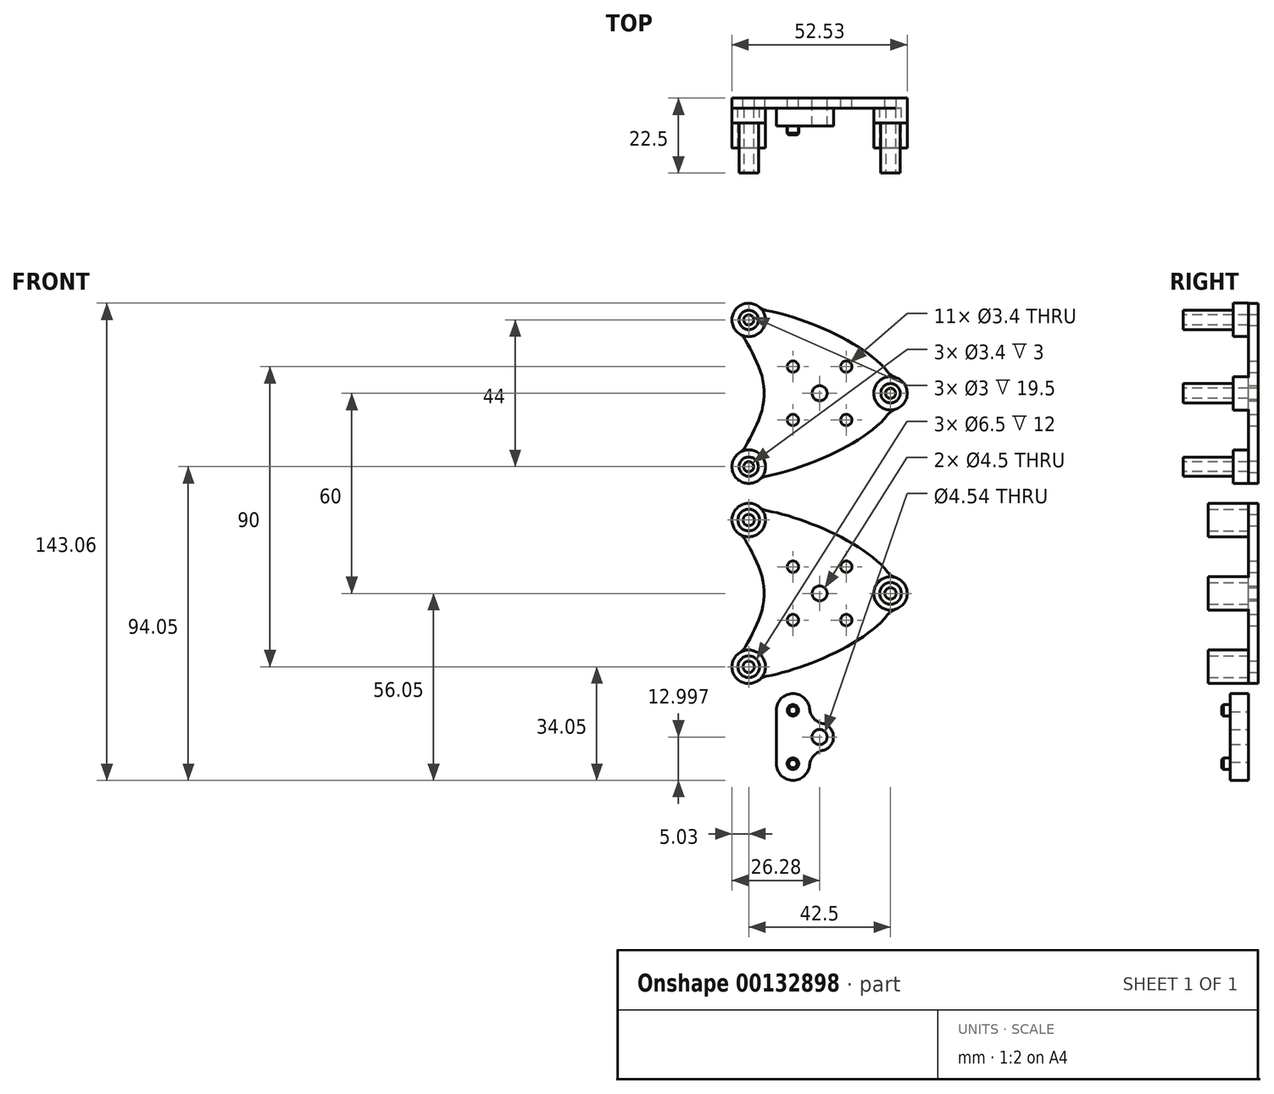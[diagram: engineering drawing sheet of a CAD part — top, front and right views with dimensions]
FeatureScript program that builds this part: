
annotation { "Feature Type Name" : "Feature", "Feature Type Description" : "" }
export const myFeature = defineFeature(function(context is Context, id is Id, definition is map)
    precondition{}
    {
        {
            var Q0;
            Q0=qCreatedBy(makeId("Front.planeOp"),FACE);
            var sketch = newSketch(context, id + "F0", { "sketchPlane" : qUnion([Q0])});
            skLineSegment(sketch, "E0", {"start": v(-21.25, 41.21) * mm, "end": v(-21.25, -41.21) * mm, "construction": true});
            skLineSegment(sketch, "E1", {"start": v(21.25, 41.21) * mm, "end": v(21.25, -41.21) * mm, "construction": true});
            skCircle(sketch, "E2", {"center": v(21.25, 0) * mm, "radius": 15.31 * mm, "construction": true});
            skPoint(sketch, "E2.centerSnap0", {"position": v(21.25, 0) * mm});
            skCircle(sketch, "E3", {"center": v(-21.25, 22) * mm, "radius": 15.31 * mm, "construction": true});
            skCircle(sketch, "E4", {"center": v(-21.25, -22) * mm, "radius": 15.31 * mm, "construction": true});
            skFitSpline(sketch, "E5", {"points": [v(-24.16, 24.83) * mm, v(22.95, 0) * mm, v(-24.16, -24.83) * mm, v(-16.56, 0) * mm, v(-24.16, 24.83) * mm]});
            skPoint(sketch, "E6", {"position": v(-54.58, 1.18) * mm});
            skPoint(sketch, "E7", {"position": v(-21.25, 0) * mm});
            skCircle(sketch, "E8", {"center": v(0, 0) * mm, "radius": 2.25 * mm});
            skCircle(sketch, "E9", {"center": v(-21.25, 22) * mm, "radius": 1.7 * mm});
            skCircle(sketch, "E10", {"center": v(-21.25, -22) * mm, "radius": 1.7 * mm});
            skCircle(sketch, "E11", {"center": v(21.25, 0) * mm, "radius": 1.7 * mm});
            skCircle(sketch, "E12", {"center": v(-21.25, -22) * mm, "radius": 3.5 * mm, "construction": true});
            skCircle(sketch, "E13", {"center": v(-8, 8) * mm, "radius": 1.7 * mm});
            skCircle(sketch, "E14.1.0.0", {"center": v(8, 8) * mm, "radius": 1.7 * mm});
            skLineSegment(sketch, "E14.direction1", {"start": v(-8, 8) * mm, "end": v(8, 8) * mm, "construction": true});
            skCircle(sketch, "E15.MirrorC", {"center": v(8, -8) * mm, "radius": 1.7 * mm});
            skCircle(sketch, "E16.MirrorC", {"center": v(-8, -8) * mm, "radius": 1.7 * mm});
            skCircle(sketch, "E17", {"center": v(-21.25, 22) * mm, "radius": 5 * mm});
            skCircle(sketch, "E18", {"center": v(-21.25, -22) * mm, "radius": 5 * mm});
            skCircle(sketch, "E19", {"center": v(21.25, 0) * mm, "radius": 5 * mm});
            skLineSegment(sketch, "E20.bottom", {"start": v(-10, 64.85) * mm, "end": v(10, 64.85) * mm, "construction": true});
            skLineSegment(sketch, "E20.top", {"start": v(-10, -64.85) * mm, "end": v(10, -64.85) * mm, "construction": true});
            skLineSegment(sketch, "E20.left", {"start": v(-10, 64.85) * mm, "end": v(-10, -64.85) * mm, "construction": true});
            skLineSegment(sketch, "E20.right", {"start": v(10, 64.85) * mm, "end": v(10, -64.85) * mm, "construction": true});
            skSolve(sketch);
        }
        {
            var Q0;
            Q0 = qSketchRegion(id + "F0", true);
            extrude(context, id + "F1", {"entities" : qUnion([Q0]), "depth" : 3 * mm});
        }
        {
            var Q0;
            {var subQ0=sQuery(id+"F0.wireOp",EDGE,"E19");var subQ1=sQuery(id+"F0.wireOp",EDGE,"E5");Q0=makeQuery(id+"F1.opExtrude","SWEPT_EDGE",EDGE,{"disambiguationData":[OSD([subQ1,subQ0]),TDD([makeQuery(id+"F0.imprint","INTERSECT",VERTEX,{"disambiguationData":[OD(1.0)],"derivedFrom":[subQ1,subQ0]})])]});}
            var Q1;
            {var subQ0=sQuery(id+"F0.wireOp",EDGE,"E19");var subQ1=sQuery(id+"F0.wireOp",EDGE,"E5");Q1=makeQuery(id+"F1.opExtrude","SWEPT_EDGE",EDGE,{"disambiguationData":[OSD([subQ1,subQ0]),TDD([makeQuery(id+"F0.imprint","INTERSECT",VERTEX,{"disambiguationData":[OD(0.0)],"derivedFrom":[subQ1,subQ0]})])]});}
            var Q2;
            {var subQ0=sQuery(id+"F0.wireOp",EDGE,"E17");var subQ1=sQuery(id+"F0.wireOp",EDGE,"E5");Q2=makeQuery(id+"F1.opExtrude","SWEPT_EDGE",EDGE,{"disambiguationData":[OSD([subQ1,subQ0]),TDD([makeQuery(id+"F0.imprint","INTERSECT",VERTEX,{"disambiguationData":[OD(1.0)],"derivedFrom":[subQ1,subQ0]})])]});}
            var Q3;
            {var subQ0=sQuery(id+"F0.wireOp",EDGE,"E18");var subQ1=sQuery(id+"F0.wireOp",EDGE,"E5");Q3=makeQuery(id+"F1.opExtrude","SWEPT_EDGE",EDGE,{"disambiguationData":[OSD([subQ1,subQ0]),TDD([makeQuery(id+"F0.imprint","INTERSECT",VERTEX,{"disambiguationData":[OD(1.0)],"derivedFrom":[subQ1,subQ0]})])]});}
            var Q4;
            {var subQ0=sQuery(id+"F0.wireOp",EDGE,"E18");var subQ1=sQuery(id+"F0.wireOp",EDGE,"E5");Q4=makeQuery(id+"F1.opExtrude","SWEPT_EDGE",EDGE,{"disambiguationData":[OSD([subQ1,subQ0]),TDD([makeQuery(id+"F0.imprint","INTERSECT",VERTEX,{"disambiguationData":[OD(0.0)],"derivedFrom":[subQ1,subQ0]})])]});}
            var Q5;
            {var subQ0=sQuery(id+"F0.wireOp",EDGE,"E17");var subQ1=sQuery(id+"F0.wireOp",EDGE,"E5");Q5=makeQuery(id+"F1.opExtrude","SWEPT_EDGE",EDGE,{"disambiguationData":[OSD([subQ1,subQ0]),TDD([makeQuery(id+"F0.imprint","INTERSECT",VERTEX,{"disambiguationData":[OD(0.0)],"derivedFrom":[subQ1,subQ0]})])]});}
            fillet(context, id + "F2", {"entities" : qUnion([Q0, Q1, Q2, Q3, Q4, Q5]), "radius" : 5 * mm, "tangentPropagation" : true, "allowEdgeOverflow" : false});
        }
        {
            var Q0;
            Q0=makeQuery(id+"F1.opExtrude","CAP_FACE",FACE,{"disambiguationData":[OSD([sQuery(id+"F0.wireOp",EDGE,"E5"),sQuery(id+"F0.wireOp",EDGE,"E8"),sQuery(id+"F0.wireOp",EDGE,"E9"),sQuery(id+"F0.wireOp",EDGE,"E10"),sQuery(id+"F0.wireOp",EDGE,"E11"),sQuery(id+"F0.wireOp",EDGE,"E13"),sQuery(id+"F0.wireOp",EDGE,"E14.1.0.0"),sQuery(id+"F0.wireOp",EDGE,"E15.MirrorC"),sQuery(id+"F0.wireOp",EDGE,"E16.MirrorC"),sQuery(id+"F0.wireOp",EDGE,"E17"),sQuery(id+"F0.wireOp",EDGE,"E18"),sQuery(id+"F0.wireOp",EDGE,"E19")])],"isStart":false});
            var sketch = newSketch(context, id + "F3", { "sketchPlane" : qUnion([Q0])});
            skCircle(sketch, "E21", {"center": v(-8, -35.05) * mm, "radius": 5 * mm});
            skCircle(sketch, "E22", {"center": v(-8, -51.05) * mm, "radius": 5 * mm});
            skLineSegment(sketch, "E23", {"start": v(-12.98, -35.46) * mm, "end": v(-12.98, -51.46) * mm});
            skLineSegment(sketch, "E24", {"start": v(-3, -34.97) * mm, "end": v(-3, -51.05) * mm});
            skCircle(sketch, "E25", {"center": v(-8, -35.05) * mm, "radius": 1.7 * mm});
            skCircle(sketch, "E26", {"center": v(-8, -51.05) * mm, "radius": 1.73 * mm});
            skCircle(sketch, "E27", {"center": v(0, -43.05) * mm, "radius": 4.14 * mm});
            skCircle(sketch, "E28", {"center": v(0, -43.05) * mm, "radius": 2.27 * mm});
            skSolve(sketch);
        }
        {
            var Q0;
            Q0 = qSketchRegion(id + "F3", true);
            extrude(context, id + "F4", {"entities" : qUnion([Q0]), "depth" : 5.4 * mm});
        }
        {
            var Q0;
            {var subQ0=sQuery(id+"F3.wireOp",EDGE,"E27");var subQ1=sQuery(id+"F3.wireOp",EDGE,"E24");Q0=makeQuery(id+"F4.opExtrude","SWEPT_EDGE",EDGE,{"disambiguationData":[OSD([subQ1,subQ0]),TDD([makeQuery(id+"F3.imprint","INTERSECT",VERTEX,{"disambiguationData":[OD(1.0)],"derivedFrom":[subQ1,subQ0]})])]});}
            var Q1;
            {var subQ0=sQuery(id+"F3.wireOp",EDGE,"E27");var subQ1=sQuery(id+"F3.wireOp",EDGE,"E24");Q1=makeQuery(id+"F4.opExtrude","SWEPT_EDGE",EDGE,{"disambiguationData":[OSD([subQ1,subQ0]),TDD([makeQuery(id+"F3.imprint","INTERSECT",VERTEX,{"disambiguationData":[OD(0.0)],"derivedFrom":[subQ1,subQ0]})])]});}
            fillet(context, id + "F5", {"entities" : qUnion([Q0, Q1]), "radius" : 5 * mm, "tangentPropagation" : true, "allowEdgeOverflow" : false});
        }
        {
            var Q0;
            Q0=makeQuery(id+"F1.opExtrude","SWEPT_BODY",BODY,{"disambiguationData":[OSD([sQuery(id+"F0.wireOp",EDGE,"E5"),sQuery(id+"F0.wireOp",EDGE,"E8"),sQuery(id+"F0.wireOp",EDGE,"E9"),sQuery(id+"F0.wireOp",EDGE,"E10"),sQuery(id+"F0.wireOp",EDGE,"E11"),sQuery(id+"F0.wireOp",EDGE,"E13"),sQuery(id+"F0.wireOp",EDGE,"E14.1.0.0"),sQuery(id+"F0.wireOp",EDGE,"E15.MirrorC"),sQuery(id+"F0.wireOp",EDGE,"E16.MirrorC"),sQuery(id+"F0.wireOp",EDGE,"E17"),sQuery(id+"F0.wireOp",EDGE,"E18"),sQuery(id+"F0.wireOp",EDGE,"E19")])]});
            transform(context, id + "F6", {"entities" : qUnion([Q0]), "transformType" : TransformType.TRANSLATION_3D, "dx" : 0 * mm, "dy" : 0 * mm, "dz" : 60 * mm, "makeCopy" : true});
        }
        {
            var Q0;
            Q0=makeQuery(id+"F1.opExtrude","CAP_FACE",FACE,{"disambiguationData":[OSD([sQuery(id+"F0.wireOp",EDGE,"E5"),sQuery(id+"F0.wireOp",EDGE,"E8"),sQuery(id+"F0.wireOp",EDGE,"E9"),sQuery(id+"F0.wireOp",EDGE,"E10"),sQuery(id+"F0.wireOp",EDGE,"E11"),sQuery(id+"F0.wireOp",EDGE,"E13"),sQuery(id+"F0.wireOp",EDGE,"E14.1.0.0"),sQuery(id+"F0.wireOp",EDGE,"E15.MirrorC"),sQuery(id+"F0.wireOp",EDGE,"E16.MirrorC"),sQuery(id+"F0.wireOp",EDGE,"E17"),sQuery(id+"F0.wireOp",EDGE,"E18"),sQuery(id+"F0.wireOp",EDGE,"E19")])],"isStart":false});
            var sketch = newSketch(context, id + "F7", { "sketchPlane" : qUnion([Q0])});
            skCircle(sketch, "E29", {"center": v(-21.25, 22) * mm, "radius": 5.02 * mm});
            skCircle(sketch, "E30", {"center": v(-21.25, -22) * mm, "radius": 5.02 * mm});
            skCircle(sketch, "E31", {"center": v(21.25, 0) * mm, "radius": 5 * mm});
            skCircle(sketch, "E32", {"center": v(-21.25, 22) * mm, "radius": 3.25 * mm});
            skCircle(sketch, "E33", {"center": v(-21.25, -22) * mm, "radius": 3.25 * mm});
            skCircle(sketch, "E34", {"center": v(21.25, 0) * mm, "radius": 3.25 * mm});
            skSolve(sketch);
        }
        {
            var Q0;
            Q0 = qSketchRegion(id + "F7", true);
            extrude(context, id + "F8", {"entities" : qUnion([Q0]), "operationType" : NewBodyOperationType.ADD, "depth" : 12 * mm});
        }
        {
            var Q0;
            Q0=makeQuery(id+"F6.opPattern","COPY",FACE,{"derivedFrom":makeQuery(id+"F1.opExtrude","CAP_FACE",FACE,{"disambiguationData":[OSD([sQuery(id+"F0.wireOp",EDGE,"E5"),sQuery(id+"F0.wireOp",EDGE,"E8"),sQuery(id+"F0.wireOp",EDGE,"E9"),sQuery(id+"F0.wireOp",EDGE,"E10"),sQuery(id+"F0.wireOp",EDGE,"E11"),sQuery(id+"F0.wireOp",EDGE,"E13"),sQuery(id+"F0.wireOp",EDGE,"E14.1.0.0"),sQuery(id+"F0.wireOp",EDGE,"E15.MirrorC"),sQuery(id+"F0.wireOp",EDGE,"E16.MirrorC"),sQuery(id+"F0.wireOp",EDGE,"E17"),sQuery(id+"F0.wireOp",EDGE,"E18"),sQuery(id+"F0.wireOp",EDGE,"E19")])],"isStart":false}),"instanceName":"1"});
            var sketch = newSketch(context, id + "F9", { "sketchPlane" : qUnion([Q0])});
            skCircle(sketch, "E35", {"center": v(-21.25, 82) * mm, "radius": 5.01 * mm});
            skCircle(sketch, "E36", {"center": v(-21.25, 38) * mm, "radius": 5.03 * mm});
            skCircle(sketch, "E37", {"center": v(21.25, 60) * mm, "radius": 5 * mm});
            skSolve(sketch);
        }
        {
            var Q0;
            Q0 = qSketchRegion(id + "F9", true);
            extrude(context, id + "F10", {"entities" : qUnion([Q0]), "operationType" : NewBodyOperationType.ADD, "depth" : 4.5 * mm});
        }
        {
            var Q0;
            Q0=makeQuery(id+"F10.opExtrude","CAP_FACE",FACE,{"disambiguationData":[OSD([sQuery(id+"F9.wireOp",EDGE,"E37")])],"isStart":false});
            var sketch = newSketch(context, id + "F11", { "sketchPlane" : qUnion([Q0])});
            skCircle(sketch, "E38", {"center": v(-21.25, 82) * mm, "radius": 2.9 * mm});
            skCircle(sketch, "E39", {"center": v(-21.25, 38) * mm, "radius": 2.9 * mm});
            skCircle(sketch, "E40", {"center": v(21.25, 60) * mm, "radius": 2.9 * mm});
            skSolve(sketch);
        }
        {
            var Q0;
            Q0 = qSketchRegion(id + "F11", true);
            extrude(context, id + "F12", {"entities" : qUnion([Q0]), "operationType" : NewBodyOperationType.ADD, "depth" : 15 * mm});
        }
        {
            var Q0;
            Q0=makeQuery(id+"F12.opExtrude","CAP_FACE",FACE,{"disambiguationData":[OSD([sQuery(id+"F11.wireOp",EDGE,"E39")])],"isStart":false});
            var sketch = newSketch(context, id + "F13", { "sketchPlane" : qUnion([Q0])});
            skCircle(sketch, "E41", {"center": v(-21.25, 82) * mm, "radius": 1.5 * mm});
            skCircle(sketch, "E42", {"center": v(21.25, 60) * mm, "radius": 1.5 * mm});
            skCircle(sketch, "E43", {"center": v(-21.25, 38) * mm, "radius": 1.5 * mm});
            skSolve(sketch);
        }
        {
            var Q0;
            Q0 = qSketchRegion(id + "F13", true);
            extrude(context, id + "F14", {"entities" : qUnion([Q0]), "operationType" : NewBodyOperationType.REMOVE, "oppositeDirection" : true, "depth" : 25 * mm});
        }
        {
            var Q0;
            Q0=makeQuery(id+"F3.imprint","IMPRINT",FACE,{"disambiguationData":[TD([[makeQuery(id+"F3.imprint","IMPRINT",EDGE,{"derivedFrom":sQuery(id+"F3.wireOp",EDGE,"E25")}),1.0]])]});
            var Q1;
            Q1=makeQuery(id+"F3.imprint","IMPRINT",FACE,{"disambiguationData":[TD([[makeQuery(id+"F3.imprint","IMPRINT",EDGE,{"derivedFrom":sQuery(id+"F3.wireOp",EDGE,"E26")}),1.0]])]});
            extrude(context, id + "F15", {"entities" : qUnion([Q0, Q1]), "operationType" : NewBodyOperationType.ADD, "depth" : 8 * mm});
        }
        {
            var Q0;
            Q0=makeQuery(id+"F15.opExtrude","CAP_EDGE",EDGE,{"disambiguationData":[OSD([sQuery(id+"F3.wireOp",EDGE,"E26")])],"isStart":false});
            var Q1;
            Q1=makeQuery(id+"F15.opExtrude","CAP_EDGE",EDGE,{"disambiguationData":[OSD([sQuery(id+"F3.wireOp",EDGE,"E25")])],"isStart":false});
            chamfer(context, id + "F16", {"entities" : qUnion([Q0, Q1]), "width" : 0.5 * mm, "tangentPropagation" : true});
        }
    });
